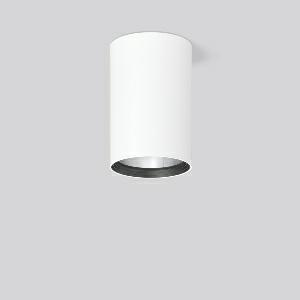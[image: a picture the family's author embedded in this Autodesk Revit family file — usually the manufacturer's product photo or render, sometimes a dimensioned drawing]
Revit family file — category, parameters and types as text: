
# Revit family: heledon_maxi_a_931231_002_66b2
name_source: partatom
category: Lighting Fixtures
units: mm (PartAtom-declared; Revit-internal decimal feet)

## family parameters
Cut with Voids When Loaded = No
Host = Face
Light Source = No
Part Type = Normal
Room Calculation Point = No
Round Connector Dimension = Use Diameter
Shared = No

## types (1)
- HELEDON maxi A (1 x LED Modul 932 fresh meat, 2150 lm, 3200)
    Apparent Load = 33 VA
    Approval mark = CE
    CIE Flux Codes = 100 100 100 100 100
    Color Rendering = 90
    Color Temperature = 3200
    Default Elevation = 1800 mm
    Description = Series: HELEDON maxi
Cylindrical surface-mounted downlight. Housing: die-cast aluminium, powder-coated. Internal ceiling frame polycarbonate with bayonet mounting. Black plastic ring and recessed LED to prevent glare from the side. Optical assembly with reflector made of MIRO-Silver with 98% total light reflection for outstanding efficiency - can be changed without tools. Special LED for illumination of meat included. Suitable for Ceiling mounting. Easy installation with a separate ceiling frame with bayonet mounting and plug connection. Driver integrated. Connected via plug-in connector. High quality converter without flickering and stroboscopic effect. The following accessories can be mounted without use of tools: interchangeable lenses, decorative glasses, honeycomb louvre, clear and frosted diffusers, white interchangeable plastic ring. 
Colour: traffic white, matt (RAL 9016)
Diameter: 123 mm
Height: 183 mm
Lamp: LED
Socket: without socket
Colour temperature: fresh meat
System power: 33 W
Rated luminous flux: 2150 lm
Luminous efficiency: 65 lm/W
Control gear: Regulated power supply
Protection class: I
Type of protection: IP 20
    Height = 183 mm
    Lamp = 1 x LED Modul 932 fresh meat
    Lamp Light Flux = 2150 lm
    Lamp count = 1
    Length = 123 mm
    Lifetime = 50000 h
    Luminous efficacy = 65 lm/W
    Manufacturer = RZB
    ModVariant = No
    Model = 931231.002
    Mounting Place = Ceiling
    Mounting Type = Surface mounted
    Number of Poles = 1
    OnlyDefault = Yes
    Power Factor = 1
    Product Name = HELEDON maxi A
    Product group = Surface mounted downlights
    ProductGroupID = 302
    Protection Class = Protection class I
    Protection Degree = IP 20
    RLX_Detail_Level = 1
    RLX_Emergency_Light_Flux = 0 lm
    RLX_Emergency_Type = 0
    RLX_Emergency_Type_DB = No
    RlxData = <blob elided: 97545 chars, md5=df8c04d4>
    Socket = socket
    Standby Power = 0 W
    System Light Flux = 2150 lm
    System Power = 33 W
    Type Comments = Product without accessories
    Type Image = 931192.002.jpg
    URL = http://relux.com
    VarID = ---
    Voltage = 230 V
    Voltage Range = 220-240 V
    Weight = 0.00 kg
    Width = 0 mm  [stored 0 ft]

note: [stored X ft] marks values corroborated as IEEE doubles in the binary element streams (Revit-internal decimal feet)

## geometry (parser evidence)
native form markers: Blend x4, Sweep x8
no freeform markers — native parametric forms only
